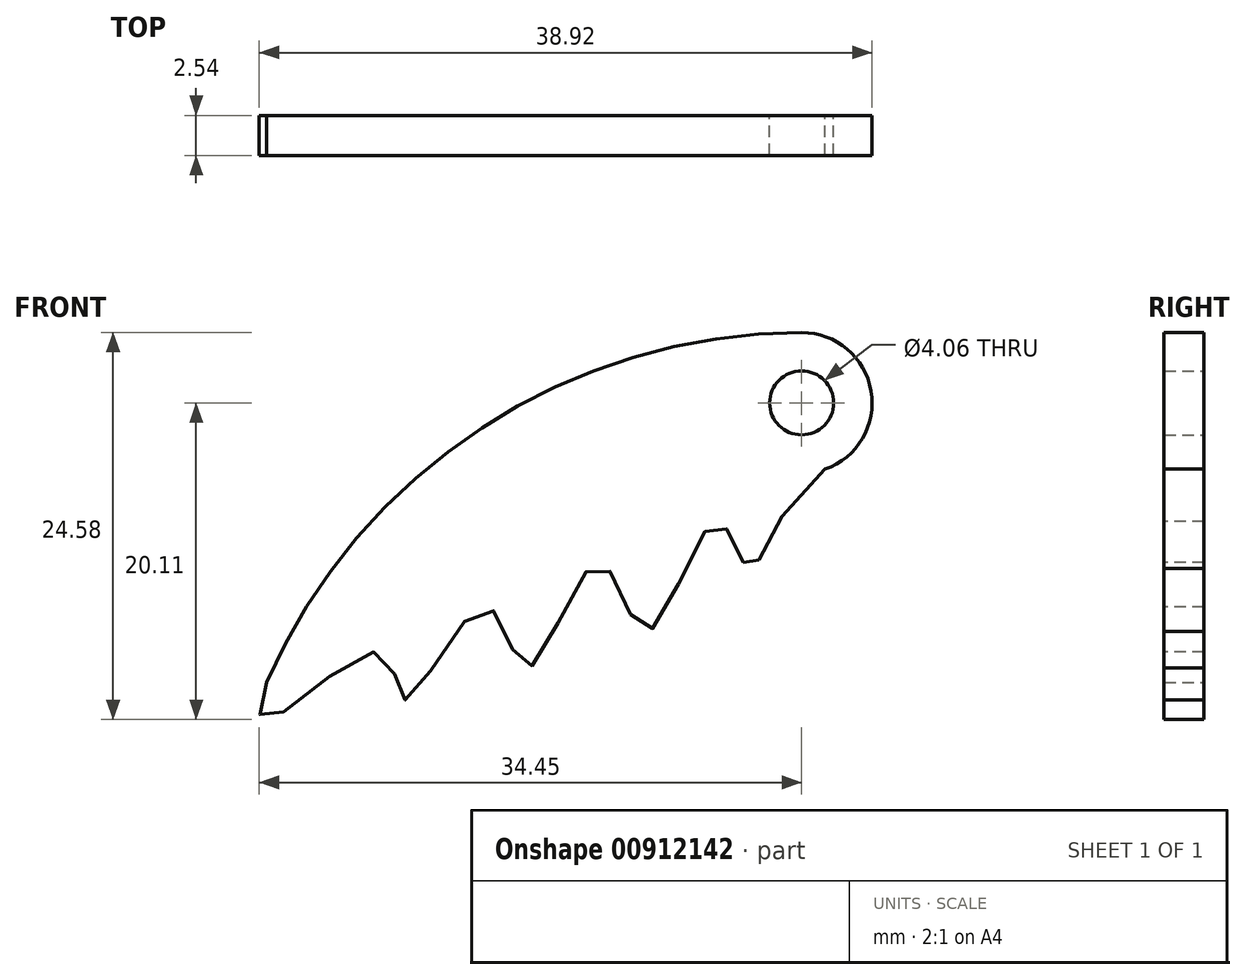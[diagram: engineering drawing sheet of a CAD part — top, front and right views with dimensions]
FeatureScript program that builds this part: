
annotation { "Feature Type Name" : "Feature", "Feature Type Description" : "" }
export const myFeature = defineFeature(function(context is Context, id is Id, definition is map)
    precondition{}
    {
        {
            var Q0;
            Q0=qCreatedBy(makeId("Front.planeOp"),FACE);
            var sketch = newSketch(context, id + "F0", { "sketchPlane" : qUnion([Q0])});
            skArc(sketch, "E0", {"start": v(1.5, -4.21) * mm, "mid": v(4.4, 0.76) * mm, "end": v(0, 4.47) * mm});
            skArc(sketch, "E1", {"start": v(0, 4.47) * mm, "mid": v(-20.3, -1.58) * mm, "end": v(-33.98, -17.76) * mm});
            skCircle(sketch, "E2", {"center": v(0, 0) * mm, "radius": 2.03 * mm});
            skFitSpline(sketch, "E3", {"points": [v(1.5, -4.21) * mm, v(-3.4, -10.47) * mm, v(-5.44, -7.54) * mm, v(-9.9, -14.53) * mm, v(-12.88, -10.13) * mm, v(-17.44, -16.84) * mm, v(-20.04, -12.95) * mm, v(-25.17, -18.87) * mm, v(-26.69, -15.88) * mm, v(-33.96, -20.11) * mm, v(-33.98, -17.76) * mm], "startDerivative": vector(-84.15, -53.77) * mm, "endDerivative": vector(26.98, 53.27) * mm});
            skSolve(sketch);
        }
        {
            var Q0;
            Q0=makeQuery(id+"F0.imprint","IMPRINT",FACE,{"disambiguationData":[TD([[makeQuery(id+"F0.imprint","IMPRINT",EDGE,{"derivedFrom":sQuery(id+"F0.wireOp",EDGE,"E0")}),1.0]])]});
            extrude(context, id + "F1", {"entities" : qUnion([Q0]), "depth" : 2.54 * mm, "offsetDistance" : 25.4 * mm});
        }
    });
